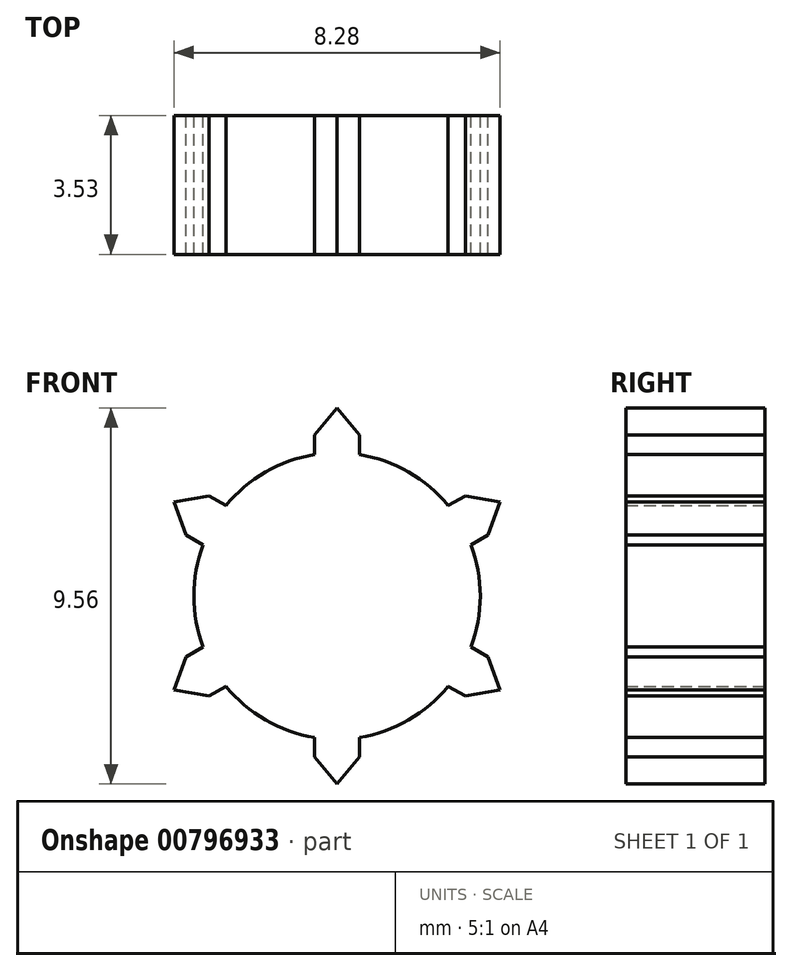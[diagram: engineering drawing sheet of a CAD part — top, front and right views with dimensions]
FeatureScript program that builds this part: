
annotation { "Feature Type Name" : "Feature", "Feature Type Description" : "" }
export const myFeature = defineFeature(function(context is Context, id is Id, definition is map)
    precondition{}
    {
        {
            var Q0;
            Q0=qCreatedBy(makeId("Front.planeOp"),FACE);
            var sketch = newSketch(context, id + "F0", { "sketchPlane" : qUnion([Q0])});
            skCircle(sketch, "E0", {"center": v(0, 0) * mm, "radius": 8.06 * mm});
            skCircle(sketch, "E1", {"center": v(0, 0) * mm, "radius": 3.64 * mm});
            skLineSegment(sketch, "E2", {"start": v(0.58, 3.6) * mm, "end": v(0.58, 4.1) * mm});
            skLineSegment(sketch, "E3", {"start": v(0.57, 4.1) * mm, "end": v(-0.57, 4.1) * mm});
            skLineSegment(sketch, "E4", {"start": v(-0.57, 4.1) * mm, "end": v(-0.57, 3.6) * mm});
            skLineSegment(sketch, "E5", {"start": v(-0.58, 4.1) * mm, "end": v(0, 4.78) * mm});
            skLineSegment(sketch, "E6", {"start": v(0, 4.78) * mm, "end": v(0.57, 4.1) * mm});
            skLineSegment(sketch, "E7.1.0", {"start": v(-3.83, 1.55) * mm, "end": v(-3.4, 1.3) * mm});
            skLineSegment(sketch, "E7.1.1", {"start": v(-2.82, 2.3) * mm, "end": v(-3.26, 2.54) * mm});
            skLineSegment(sketch, "E7.1.2", {"start": v(-3.83, 1.55) * mm, "end": v(-4.14, 2.39) * mm});
            skLineSegment(sketch, "E7.1.3", {"start": v(-4.14, 2.39) * mm, "end": v(-3.26, 2.54) * mm});
            skLineSegment(sketch, "E7.1.4", {"start": v(-3.26, 2.54) * mm, "end": v(-3.83, 1.55) * mm});
            skLineSegment(sketch, "E7.2.0", {"start": v(-3.26, -2.54) * mm, "end": v(-2.82, -2.3) * mm});
            skLineSegment(sketch, "E7.2.1", {"start": v(-3.4, -1.3) * mm, "end": v(-3.83, -1.55) * mm});
            skLineSegment(sketch, "E7.2.2", {"start": v(-3.26, -2.54) * mm, "end": v(-4.14, -2.39) * mm});
            skLineSegment(sketch, "E7.2.3", {"start": v(-4.14, -2.39) * mm, "end": v(-3.83, -1.55) * mm});
            skLineSegment(sketch, "E7.2.4", {"start": v(-3.83, -1.55) * mm, "end": v(-3.26, -2.54) * mm});
            skLineSegment(sketch, "E7.3.0", {"start": v(0.57, -4.1) * mm, "end": v(0.57, -3.6) * mm});
            skLineSegment(sketch, "E7.3.1", {"start": v(-0.58, -3.6) * mm, "end": v(-0.58, -4.1) * mm});
            skLineSegment(sketch, "E7.3.2", {"start": v(0.58, -4.1) * mm, "end": v(0, -4.78) * mm});
            skLineSegment(sketch, "E7.3.3", {"start": v(0, -4.78) * mm, "end": v(-0.58, -4.1) * mm});
            skLineSegment(sketch, "E7.3.4", {"start": v(-0.58, -4.1) * mm, "end": v(0.57, -4.1) * mm});
            skLineSegment(sketch, "E7.4.0", {"start": v(3.83, -1.55) * mm, "end": v(3.4, -1.3) * mm});
            skLineSegment(sketch, "E7.4.1", {"start": v(2.82, -2.3) * mm, "end": v(3.26, -2.54) * mm});
            skLineSegment(sketch, "E7.4.2", {"start": v(3.83, -1.55) * mm, "end": v(4.14, -2.39) * mm});
            skLineSegment(sketch, "E7.4.3", {"start": v(4.14, -2.39) * mm, "end": v(3.26, -2.54) * mm});
            skLineSegment(sketch, "E7.4.4", {"start": v(3.26, -2.54) * mm, "end": v(3.83, -1.55) * mm});
            skLineSegment(sketch, "E7.5.0", {"start": v(3.26, 2.54) * mm, "end": v(2.82, 2.3) * mm});
            skLineSegment(sketch, "E7.5.1", {"start": v(3.4, 1.3) * mm, "end": v(3.83, 1.55) * mm});
            skLineSegment(sketch, "E7.5.2", {"start": v(3.26, 2.54) * mm, "end": v(4.14, 2.39) * mm});
            skLineSegment(sketch, "E7.5.3", {"start": v(4.14, 2.39) * mm, "end": v(3.83, 1.55) * mm});
            skLineSegment(sketch, "E7.5.4", {"start": v(3.83, 1.55) * mm, "end": v(3.26, 2.54) * mm});
            skSolve(sketch);
        }
        {
            var Q0;
            {var subQ0=sQuery(id+"F0.wireOp",EDGE,"E1");var subQ8=makeQuery(id+"F0.imprint","INTERSECT",VERTEX,{"derivedFrom":[subQ0,sQuery(id+"F0.wireOp",EDGE,"E7.5.0")]});Q0=makeQuery(id+"F0.imprint","IMPRINT",FACE,{"disambiguationData":[TD([[makeQuery(id+"F0.imprint","IMPRINT",EDGE,{"disambiguationData":[TD([[subQ8,1.0]])],"derivedFrom":subQ0}),1.0]])]});}
            var Q1;
            {var subQ0=sQuery(id+"F0.wireOp",EDGE,"E7.2.0");Q1=makeQuery(id+"F0.imprint","IMPRINT",FACE,{"disambiguationData":[TD([[makeQuery(id+"F0.imprint","IMPRINT",EDGE,{"derivedFrom":subQ0}),1.0]])]});}
            var Q2;
            Q2=makeQuery(id+"F0.imprint","IMPRINT",FACE,{"disambiguationData":[TD([[makeQuery(id+"F0.imprint","IMPRINT",EDGE,{"derivedFrom":sQuery(id+"F0.wireOp",EDGE,"E7.2.2")}),-1.0]])]});
            var Q3;
            Q3=makeQuery(id+"F0.imprint","IMPRINT",FACE,{"disambiguationData":[TD([[makeQuery(id+"F0.imprint","IMPRINT",EDGE,{"derivedFrom":sQuery(id+"F0.wireOp",EDGE,"E7.3.2")}),-1.0]])]});
            var Q4;
            {var subQ0=sQuery(id+"F0.wireOp",EDGE,"E7.3.0");Q4=makeQuery(id+"F0.imprint","IMPRINT",FACE,{"disambiguationData":[TD([[makeQuery(id+"F0.imprint","IMPRINT",EDGE,{"derivedFrom":subQ0}),1.0]])]});}
            var Q5;
            Q5=makeQuery(id+"F0.imprint","IMPRINT",FACE,{"disambiguationData":[TD([[makeQuery(id+"F0.imprint","IMPRINT",EDGE,{"derivedFrom":sQuery(id+"F0.wireOp",EDGE,"E7.4.2")}),-1.0]])]});
            var Q6;
            {var subQ0=sQuery(id+"F0.wireOp",EDGE,"E7.4.0");Q6=makeQuery(id+"F0.imprint","IMPRINT",FACE,{"disambiguationData":[TD([[makeQuery(id+"F0.imprint","IMPRINT",EDGE,{"derivedFrom":subQ0}),1.0]])]});}
            var Q7;
            Q7=makeQuery(id+"F0.imprint","IMPRINT",FACE,{"disambiguationData":[TD([[makeQuery(id+"F0.imprint","IMPRINT",EDGE,{"derivedFrom":sQuery(id+"F0.wireOp",EDGE,"E7.1.2")}),-1.0]])]});
            var Q8;
            Q8=makeQuery(id+"F0.imprint","IMPRINT",FACE,{"disambiguationData":[TD([[makeQuery(id+"F0.imprint","IMPRINT",EDGE,{"derivedFrom":sQuery(id+"F0.wireOp",EDGE,"E7.5.2")}),-1.0]])]});
            var Q9;
            {var subQ0=sQuery(id+"F0.wireOp",EDGE,"E7.5.0");Q9=makeQuery(id+"F0.imprint","IMPRINT",FACE,{"disambiguationData":[TD([[makeQuery(id+"F0.imprint","IMPRINT",EDGE,{"derivedFrom":subQ0}),1.0]])]});}
            var Q10;
            {var subQ0=sQuery(id+"F0.wireOp",EDGE,"E2");Q10=makeQuery(id+"F0.imprint","IMPRINT",FACE,{"disambiguationData":[TD([[makeQuery(id+"F0.imprint","IMPRINT",EDGE,{"derivedFrom":subQ0}),1.0]])]});}
            var Q11;
            {var subQ0=sQuery(id+"F0.wireOp",EDGE,"E7.1.0");Q11=makeQuery(id+"F0.imprint","IMPRINT",FACE,{"disambiguationData":[TD([[makeQuery(id+"F0.imprint","IMPRINT",EDGE,{"derivedFrom":subQ0}),1.0]])]});}
            var Q12;
            Q12=makeQuery(id+"F0.imprint","IMPRINT",FACE,{"disambiguationData":[TD([[makeQuery(id+"F0.imprint","IMPRINT",EDGE,{"derivedFrom":sQuery(id+"F0.wireOp",EDGE,"E3")}),-1.0]])]});
            extrude(context, id + "F1", {"entities" : qUnion([Q0, Q1, Q2, Q3, Q4, Q5, Q6, Q7, Q8, Q9, Q10, Q11, Q12]), "depth" : 5 * mm, "offsetDistance" : 25 * mm, "hasSecondDirection" : true, "secondDirectionOppositeDirection" : false, "secondDirectionDepth" : 1.48 * mm});
        }
    });
